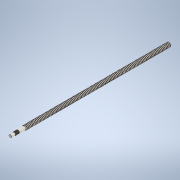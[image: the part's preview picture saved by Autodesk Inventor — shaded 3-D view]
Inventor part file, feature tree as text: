
AUTODESK INVENTOR PART (.ipt)
format: ipt  version: 2020.1 (Build 241239000, 239)  size: 3,731,968 bytes
history: native  units: mm
features: other x2, extrude x1, sketch x1
ambient origin geometry x8: Origin, YZ Plane, XZ Plane, XY Plane, X Axis, Y Axis, Z Axis, Center Point
bodies: Body1 (feature_tree)
feature tree (4):
  other  "Твердое тело1"
  extrude  "Выдавливание1"  Depth=200.0mm TaperAngle=0.0deg
  sketch  "Эскиз1"
  other  "Aesthetic Chamfer"
